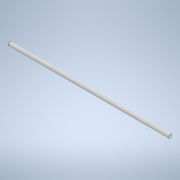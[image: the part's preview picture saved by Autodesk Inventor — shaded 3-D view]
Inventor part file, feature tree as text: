
AUTODESK INVENTOR PART (.ipt)
format: ipt  version: 2021 (Build 250183000, 183)  size: 90,624 bytes
history: native  units: in
note: dims shown in document units (in); Inventor stores cm internally (conversion verified against a paired STEP export)
features: extrude x1, sketch x1
ambient origin geometry x8: Origin, YZ Plane, XZ Plane, XY Plane, X Axis, Y Axis, Z Axis, Center Point
bodies: Solid1 (feature_tree)
feature tree (2):
  extrude  "Extrusion1"  Depth=13.7795in TaperAngle=0.0deg
  sketch  "Sketch1"  dims[d0=0.315in d1=13.7795in d2=0.0in]
